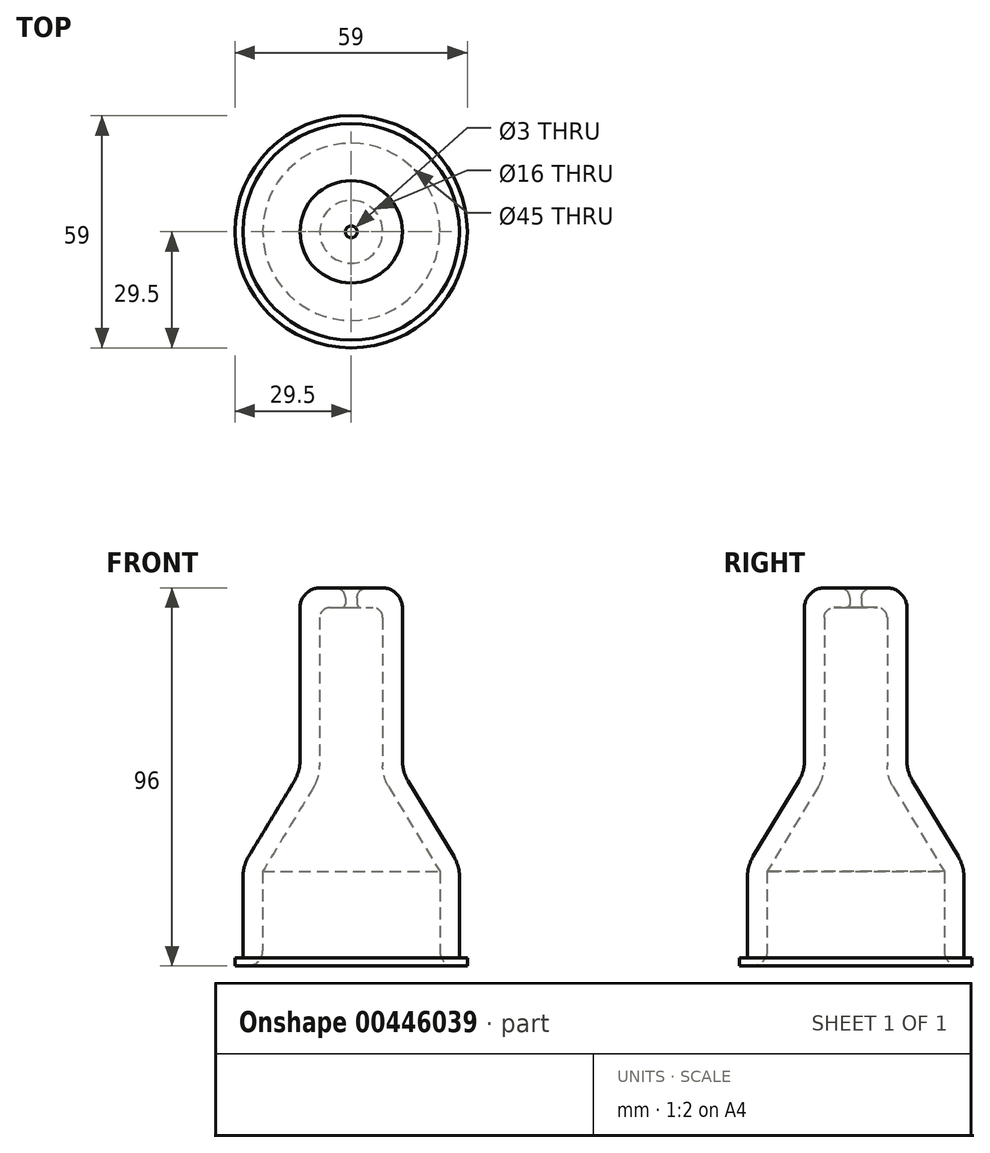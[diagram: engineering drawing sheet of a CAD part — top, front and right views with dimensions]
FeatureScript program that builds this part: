
annotation { "Feature Type Name" : "Feature", "Feature Type Description" : "" }
export const myFeature = defineFeature(function(context is Context, id is Id, definition is map)
    precondition{}
    {
        {
            var Q0;
            Q0=qCreatedBy(makeId("Front.planeOp"),FACE);
            var sketch = newSketch(context, id + "F0", { "sketchPlane" : qUnion([Q0])});
            skLineSegment(sketch, "E0", {"start": v(22.5, 3.75) * mm, "end": v(22.5, 24) * mm});
            skLineSegment(sketch, "E1", {"start": v(22.5, 24) * mm, "end": v(9.44, 45.62) * mm});
            skLineSegment(sketch, "E2", {"start": v(8, 50.79) * mm, "end": v(8, 88.5) * mm});
            skLineSegment(sketch, "E3", {"start": v(5.5, 91) * mm, "end": v(2.5, 91) * mm});
            skLineSegment(sketch, "E4", {"start": v(4, 96) * mm, "end": v(8, 96) * mm});
            skLineSegment(sketch, "E5", {"start": v(13, 91) * mm, "end": v(13, 52.18) * mm});
            skLineSegment(sketch, "E6", {"start": v(14.44, 47) * mm, "end": v(26.06, 27.78) * mm});
            skLineSegment(sketch, "E7", {"start": v(27.5, 0) * mm, "end": v(26.25, 0) * mm});
            skPoint(sketch, "E8.visualSharp", {"position": v(8, 48) * mm});
            skArc(sketch, "E8.filletArc", {"start": v(8, 50.79) * mm, "mid": v(8.37, 48.1) * mm, "end": v(9.44, 45.62) * mm});
            skPoint(sketch, "E9.visualSharp", {"position": v(13, 96) * mm});
            skArc(sketch, "E9.filletArc", {"start": v(13, 91) * mm, "mid": v(11.54, 94.54) * mm, "end": v(8, 96) * mm});
            skArc(sketch, "E10.filletArc", {"start": v(27.5, 22.6) * mm, "mid": v(27.13, 25.3) * mm, "end": v(26.06, 27.78) * mm});
            skLineSegment(sketch, "E11", {"start": v(1.5, 92) * mm, "end": v(1.5, 93.5) * mm});
            skLineSegment(sketch, "E12", {"start": v(27.5, 0) * mm, "end": v(29.5, 0) * mm});
            skLineSegment(sketch, "E13", {"start": v(29.5, 0) * mm, "end": v(29.5, 2) * mm});
            skLineSegment(sketch, "E14", {"start": v(29.5, 2) * mm, "end": v(28, 2) * mm});
            skLineSegment(sketch, "E15", {"start": v(27.5, 22.6) * mm, "end": v(27.5, 2.5) * mm});
            skPoint(sketch, "E16.visualSharp", {"position": v(13, 49.4) * mm});
            skArc(sketch, "E16.filletArc", {"start": v(13, 52.18) * mm, "mid": v(13.37, 49.5) * mm, "end": v(14.44, 47) * mm});
            skPoint(sketch, "E17.visualSharp", {"position": v(27.5, 2) * mm});
            skArc(sketch, "E17.filletArc", {"start": v(27.5, 2.5) * mm, "mid": v(27.65, 2.15) * mm, "end": v(28, 2) * mm});
            skPoint(sketch, "E18.visualSharp", {"position": v(1.5, 96) * mm});
            skArc(sketch, "E18.filletArc", {"start": v(4, 96) * mm, "mid": v(2.23, 95.27) * mm, "end": v(1.5, 93.5) * mm});
            skPoint(sketch, "E19.visualSharp", {"position": v(1.5, 91) * mm});
            skArc(sketch, "E19.filletArc", {"start": v(1.5, 92) * mm, "mid": v(1.8, 91.3) * mm, "end": v(2.5, 91) * mm});
            skPoint(sketch, "E20.visualSharp", {"position": v(22.5, 0) * mm});
            skArc(sketch, "E20.filletArc", {"start": v(22.5, 3.75) * mm, "mid": v(23.6, 1.1) * mm, "end": v(26.25, 0) * mm});
            skArc(sketch, "E21.filletArc", {"start": v(8, 88.5) * mm, "mid": v(7.27, 90.27) * mm, "end": v(5.5, 91) * mm});
            skSolve(sketch);
        }
        {
            var Q0;
            Q0=qCreatedBy(makeId("Front.planeOp"),FACE);
            var sketch = newSketch(context, id + "F1", { "sketchPlane" : qUnion([Q0])});
            skLineSegment(sketch, "E22", {"start": v(0, 0) * mm, "end": v(0, 26.94) * mm, "construction": true});
            skSolve(sketch);
        }
        {
            var Q0;
            Q0=makeQuery(id+"F0.imprint","IMPRINT",FACE,{"disambiguationData":[TD([[makeQuery(id+"F0.imprint","IMPRINT",EDGE,{"derivedFrom":sQuery(id+"F0.wireOp",EDGE,"E0")}),-1.0]])]});
            var Q1;
            Q1=sQuery(id+"F1.wireOp",EDGE,"E22");
            revolve(context, id + "F2", {"entities" : qUnion([Q0]), "axis" : qUnion([Q1]), "revolveType" : RevolveType.FULL});
        }
    });
